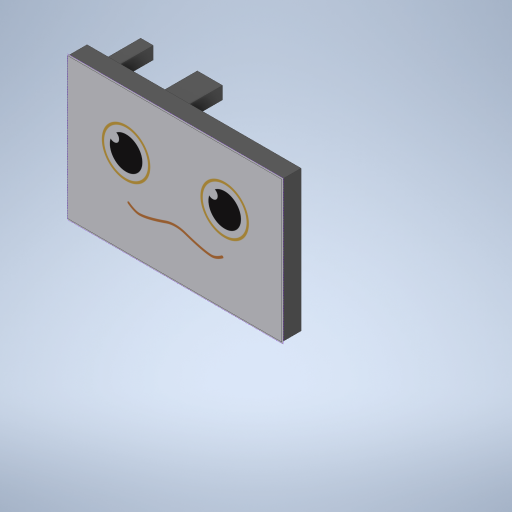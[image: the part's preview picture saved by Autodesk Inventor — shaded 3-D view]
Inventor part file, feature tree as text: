
AUTODESK INVENTOR PART (.ipt)
format: ipt  version: 2023 (Build 270158000, 158)  size: 477,184 bytes
history: native  units: mm
features: extrude x6, sketch x6, projected_geometry x2, fillet x1, other x1
ambient origin geometry x8: Origin, YZ Plane, XZ Plane, XY Plane, X Axis, Y Axis, Z Axis, Center Point
bodies: Body1 (feature_tree)
feature tree (16):
  extrude  "돌출2"  Depth=85.0mm
  extrude  "돌출3"  Depth=56.0mm
  sketch  "스케치5"
  extrude  "돌출4"  Depth=7.65mm TaperAngle=0.0deg
  fillet  "모깎기1"  Radius=5.0mm
  extrude  "돌출5"  Depth=5.0mm
  extrude  "돌출6"  Depth=0.6mm
  extrude  "돌출7"  Depth=0.6mm
  sketch  "스케치9"
  sketch  "스케치2"
  sketch  "스케치4"
  sketch  "스케치6"
  projected_geometry  "투영된 루프1"
  sketch  "스케치7"
  projected_geometry  "투영된 루프2"
  other  "이미지1"
